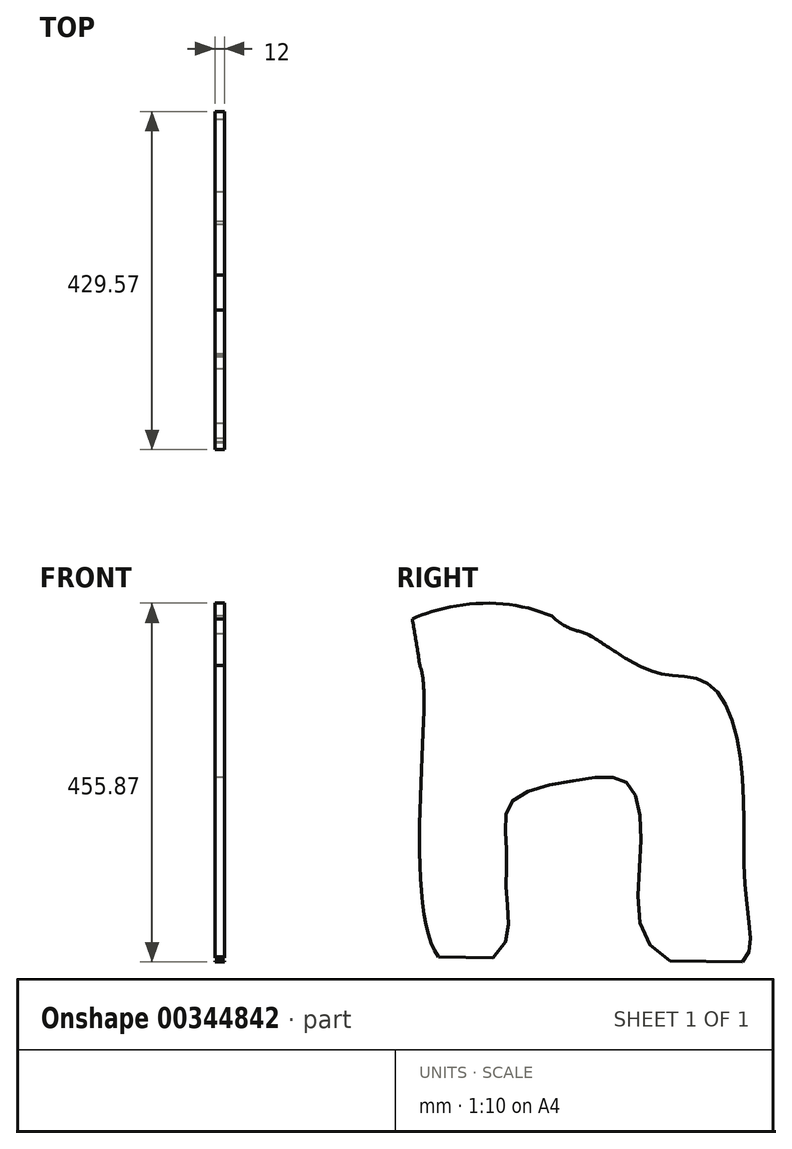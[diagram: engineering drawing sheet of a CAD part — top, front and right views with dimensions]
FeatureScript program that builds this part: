
annotation { "Feature Type Name" : "Feature", "Feature Type Description" : "" }
export const myFeature = defineFeature(function(context is Context, id is Id, definition is map)
    precondition{}
    {
        {
            var Q0;
            Q0=qCreatedBy(makeId("Right.planeOp"),FACE);
            var sketch = newSketch(context, id + "F0", { "sketchPlane" : qUnion([Q0])});
            skPoint(sketch, "E0.middle", {"position": v(0, 0) * mm});
            skFitSpline(sketch, "E1", {"points": [v(-174.24, -149.09) * mm, v(-197, 190.33) * mm, v(-214.6, 242.07) * mm, v(-234.26, 265.87) * mm, v(-95.23, 303.99) * mm, v(63.1, 232.58) * mm, v(112.76, 213.96) * mm, v(165.54, 201.54) * mm, v(205.9, 102.2) * mm, v(212.1, -68.55) * mm, v(205.9, -152.36) * mm, v(94.14, -134.33) * mm, v(78.62, 0) * mm, v(59.99, 77.36) * mm, v(0, 80.47) * mm, v(-85.92, 52.53) * mm, v(-92.13, 0) * mm, v(-92.13, -68.55) * mm, v(-98.34, -134.33) * mm, v(-174.24, -149.09) * mm]});
            skFitSpline(sketch, "E2", {"points": [v(-197, 190.33) * mm, v(-234.26, 373.84) * mm, v(-276.84, 435.92) * mm, v(-314.1, 451.45) * mm, v(-331.86, 505.38) * mm, v(-272.59, 514.16) * mm, v(-234.26, 551.72) * mm, v(-197, 536.05) * mm, v(-175.88, 507.34) * mm, v(-34.31, 288.37) * mm, v(10.3, 265.87) * mm, v(63.1, 232.58) * mm], "startDerivative": vector(-201.1, 1403.66) * mm, "endDerivative": vector(664.26, -489.03) * mm});
            skLineSegment(sketch, "E3", {"start": v(-178.44, -144.2) * mm, "end": v(-109.15, -145.43) * mm});
            skPoint(sketch, "E4.orphan", {"position": v(284.08, -152.36) * mm});
            skLineSegment(sketch, "E5.trimOffspring", {"start": v(115.29, -149.39) * mm, "end": v(207.57, -151.01) * mm});
            skSolve(sketch);
        }
        {
            var Q0;
            {var subQ1=sQuery(id+"F0.wireOp",EDGE,"E1");Q0=makeQuery(id+"F0.imprint","IMPRINT",FACE,{"disambiguationData":[TD([[makeQuery(id+"F0.imprint","IMPRINT",EDGE,{"derivedFrom":subQ1}),-1.0]])]});}
            extrude(context, id + "F1", {"entities" : qUnion([Q0]), "depth" : 12 * mm});
        }
    });
